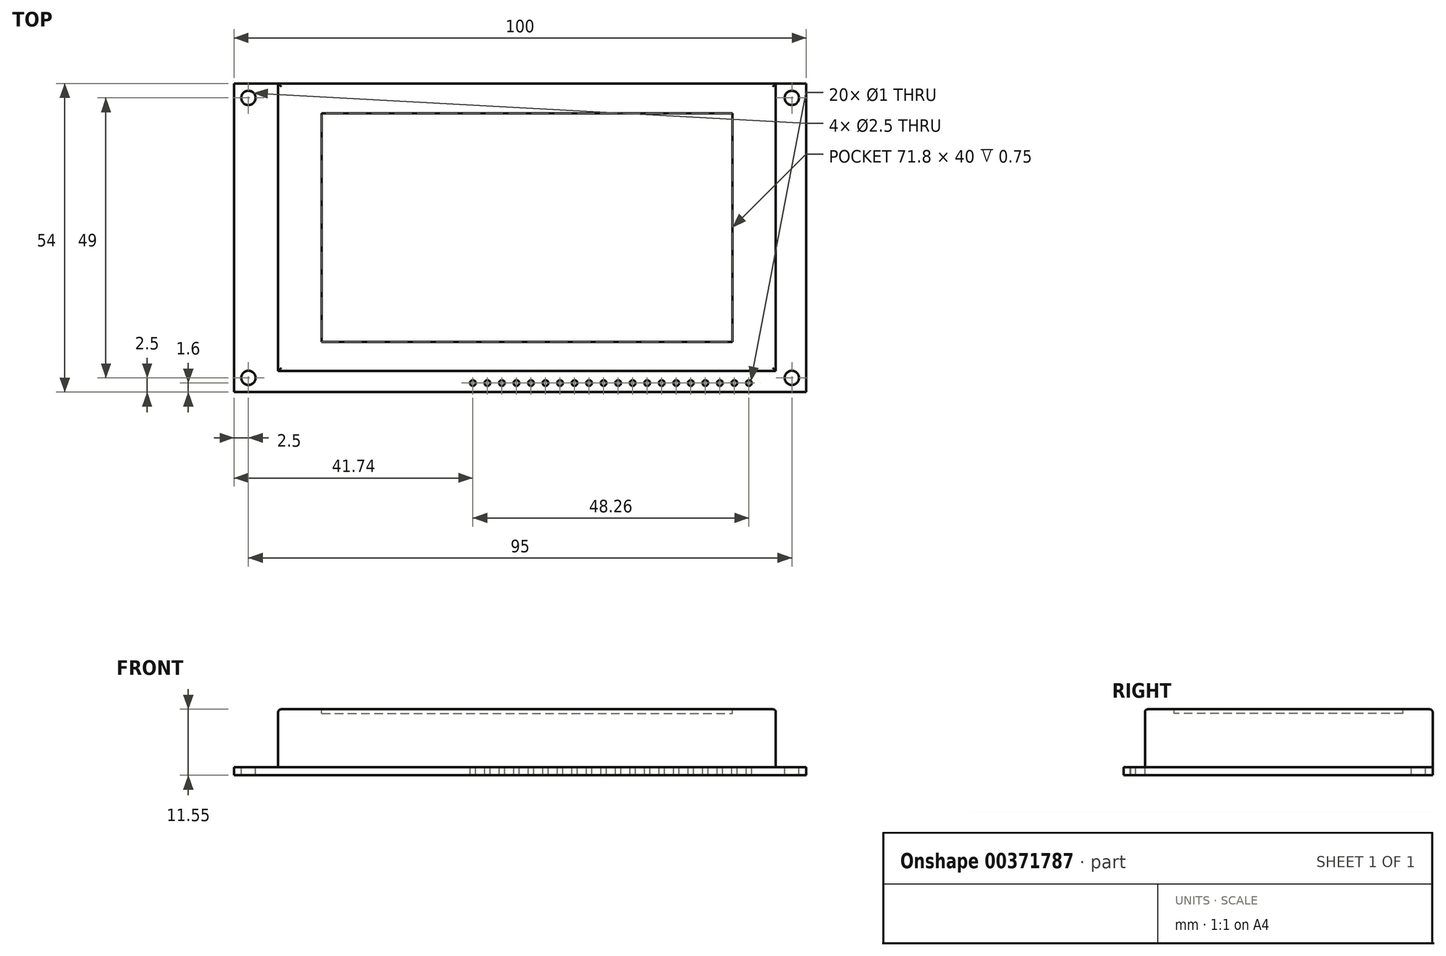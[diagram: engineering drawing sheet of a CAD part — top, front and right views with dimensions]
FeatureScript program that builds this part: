
annotation { "Feature Type Name" : "Feature", "Feature Type Description" : "" }
export const myFeature = defineFeature(function(context is Context, id is Id, definition is map)
    precondition{}
    {
        {
            var Q0;
            Q0=qCreatedBy(makeId("Top.planeOp"),FACE);
            var sketch = newSketch(context, id + "F0", { "sketchPlane" : qUnion([Q0])});
            skLineSegment(sketch, "E0.bottom", {"start": v(0, 0) * mm, "end": v(100, 0) * mm});
            skLineSegment(sketch, "E0.top", {"start": v(0, 54) * mm, "end": v(100, 54) * mm});
            skLineSegment(sketch, "E0.left", {"start": v(0, 0) * mm, "end": v(0, 54) * mm});
            skLineSegment(sketch, "E0.right", {"start": v(100, 0) * mm, "end": v(100, 54) * mm});
            skSolve(sketch);
        }
        {
            var Q0;
            Q0=makeQuery(id+"F0.imprint","IMPRINT",FACE,{"disambiguationData":[TD([[makeQuery(id+"F0.imprint","IMPRINT",EDGE,{"derivedFrom":sQuery(id+"F0.wireOp",EDGE,"E0.bottom")}),1.0]])]});
            extrude(context, id + "F1", {"entities" : qUnion([Q0]), "depth" : 1.45 * mm});
        }
        {
            var Q0;
            Q0=makeQuery(id+"F1.opExtrude","CAP_FACE",FACE,{"disambiguationData":[OSD([sQuery(id+"F0.wireOp",EDGE,"E0.bottom"),sQuery(id+"F0.wireOp",EDGE,"E0.top"),sQuery(id+"F0.wireOp",EDGE,"E0.left"),sQuery(id+"F0.wireOp",EDGE,"E0.right")])],"isStart":false});
            var sketch = newSketch(context, id + "F2", { "sketchPlane" : qUnion([Q0])});
            skLineSegment(sketch, "E1.bottom", {"start": v(7.7, 54) * mm, "end": v(94.7, 54) * mm});
            skLineSegment(sketch, "E1.top", {"start": v(7.7, 3.7) * mm, "end": v(94.7, 3.7) * mm});
            skLineSegment(sketch, "E1.left", {"start": v(7.7, 54) * mm, "end": v(7.7, 3.7) * mm});
            skLineSegment(sketch, "E1.right", {"start": v(94.7, 54) * mm, "end": v(94.7, 3.7) * mm});
            skSolve(sketch);
        }
        {
            var Q0;
            Q0=makeQuery(id+"F2.imprint","IMPRINT",FACE,{"disambiguationData":[TD([[makeQuery(id+"F2.imprint","IMPRINT",EDGE,{"derivedFrom":sQuery(id+"F2.wireOp",EDGE,"E1.bottom")}),-1.0]])]});
            extrude(context, id + "F3", {"entities" : qUnion([Q0]), "operationType" : NewBodyOperationType.ADD, "depth" : 10.1 * mm});
        }
        {
            var Q0;
            Q0=makeQuery(id+"F1.opExtrude","CAP_FACE",FACE,{"disambiguationData":[OSD([sQuery(id+"F0.wireOp",EDGE,"E0.bottom"),sQuery(id+"F0.wireOp",EDGE,"E0.top"),sQuery(id+"F0.wireOp",EDGE,"E0.left"),sQuery(id+"F0.wireOp",EDGE,"E0.right")])],"isStart":false});
            var sketch = newSketch(context, id + "F4", { "sketchPlane" : qUnion([Q0])});
            skLineSegment(sketch, "E2.bottom", {"start": v(2.5, 51.5) * mm, "end": v(97.5, 51.5) * mm, "construction": true});
            skLineSegment(sketch, "E2.top", {"start": v(2.5, 2.5) * mm, "end": v(97.5, 2.5) * mm, "construction": true});
            skLineSegment(sketch, "E2.left", {"start": v(2.5, 51.5) * mm, "end": v(2.5, 2.5) * mm, "construction": true});
            skLineSegment(sketch, "E2.right", {"start": v(97.5, 51.5) * mm, "end": v(97.5, 2.5) * mm, "construction": true});
            skCircle(sketch, "E3", {"center": v(2.5, 51.5) * mm, "radius": 1.25 * mm});
            skCircle(sketch, "E4", {"center": v(2.5, 2.5) * mm, "radius": 1.25 * mm});
            skCircle(sketch, "E5", {"center": v(97.5, 2.5) * mm, "radius": 1.25 * mm});
            skCircle(sketch, "E6", {"center": v(97.5, 51.5) * mm, "radius": 1.25 * mm});
            skSolve(sketch);
        }
        {
            var Q0;
            Q0 = qSketchRegion(id + "F4", true);
            extrude(context, id + "F5", {"entities" : qUnion([Q0]), "operationType" : NewBodyOperationType.REMOVE, "endBound" : BoundingType.THROUGH_ALL, "oppositeDirection" : true, "depth" : 25 * mm});
        }
        {
            var Q0;
            Q0=makeQuery(id+"F3.opExtrude","CAP_FACE",FACE,{"disambiguationData":[OSD([sQuery(id+"F2.wireOp",EDGE,"E1.bottom"),sQuery(id+"F2.wireOp",EDGE,"E1.top"),sQuery(id+"F2.wireOp",EDGE,"E1.left"),sQuery(id+"F2.wireOp",EDGE,"E1.right")])],"isStart":false});
            var sketch = newSketch(context, id + "F6", { "sketchPlane" : qUnion([Q0])});
            skLineSegment(sketch, "E7.bottom", {"start": v(15.3, 48.8) * mm, "end": v(87.1, 48.8) * mm});
            skLineSegment(sketch, "E7.top", {"start": v(15.3, 8.8) * mm, "end": v(87.1, 8.8) * mm});
            skLineSegment(sketch, "E7.left", {"start": v(15.3, 48.8) * mm, "end": v(15.3, 8.8) * mm});
            skLineSegment(sketch, "E7.right", {"start": v(87.1, 48.8) * mm, "end": v(87.1, 8.8) * mm});
            skLineSegment(sketch, "E8", {"start": v(87.1, 8.8) * mm, "end": v(15.3, 48.8) * mm, "construction": true});
            skPoint(sketch, "E9", {"position": v(51.2, 28.8) * mm});
            skSolve(sketch);
        }
        {
            var Q0;
            Q0=makeQuery(id+"F3.opExtrude","CAP_EDGE",EDGE,{"disambiguationData":[OSD([sQuery(id+"F2.wireOp",EDGE,"E1.left")])],"isStart":false});
            var Q1;
            Q1=makeQuery(id+"F3.opExtrude","CAP_EDGE",EDGE,{"disambiguationData":[OSD([sQuery(id+"F2.wireOp",EDGE,"E1.bottom")])],"isStart":false});
            var Q2;
            Q2=makeQuery(id+"F3.opExtrude","CAP_EDGE",EDGE,{"disambiguationData":[OSD([sQuery(id+"F2.wireOp",EDGE,"E1.top")])],"isStart":false});
            var Q3;
            Q3=makeQuery(id+"F3.opExtrude","CAP_EDGE",EDGE,{"disambiguationData":[OSD([sQuery(id+"F2.wireOp",EDGE,"E1.right")])],"isStart":false});
            fillet(context, id + "F7", {"entities" : qUnion([Q0, Q1, Q2, Q3]), "radius" : 0.5 * mm, "tangentPropagation" : true, "allowEdgeOverflow" : false});
        }
        {
            var Q0;
            Q0=makeQuery(id+"F6.imprint","IMPRINT",FACE,{"disambiguationData":[TD([[makeQuery(id+"F6.imprint","IMPRINT",EDGE,{"derivedFrom":sQuery(id+"F6.wireOp",EDGE,"E7.bottom")}),-1.0]])]});
            extrude(context, id + "F8", {"entities" : qUnion([Q0]), "operationType" : NewBodyOperationType.REMOVE, "oppositeDirection" : true, "depth" : .75 * mm});
        }
        {
            var Q0;
            Q0=makeQuery(id+"F1.opExtrude","CAP_FACE",FACE,{"disambiguationData":[OSD([sQuery(id+"F0.wireOp",EDGE,"E0.bottom"),sQuery(id+"F0.wireOp",EDGE,"E0.top"),sQuery(id+"F0.wireOp",EDGE,"E0.left"),sQuery(id+"F0.wireOp",EDGE,"E0.right")])],"isStart":false});
            var sketch = newSketch(context, id + "F9", { "sketchPlane" : qUnion([Q0])});
            skCircle(sketch, "E10", {"center": v(90, 1.6) * mm, "radius": 0.5 * mm});
            skCircle(sketch, "E11.1.0.0", {"center": v(87.46, 1.6) * mm, "radius": 0.5 * mm});
            skCircle(sketch, "E11.2.0.0", {"center": v(84.92, 1.6) * mm, "radius": 0.5 * mm});
            skCircle(sketch, "E11.3.0.0", {"center": v(82.38, 1.6) * mm, "radius": 0.5 * mm});
            skCircle(sketch, "E11.4.0.0", {"center": v(79.84, 1.6) * mm, "radius": 0.5 * mm});
            skCircle(sketch, "E11.5.0.0", {"center": v(77.3, 1.6) * mm, "radius": 0.5 * mm});
            skCircle(sketch, "E11.6.0.0", {"center": v(74.76, 1.6) * mm, "radius": 0.5 * mm});
            skCircle(sketch, "E11.7.0.0", {"center": v(72.22, 1.6) * mm, "radius": 0.5 * mm});
            skCircle(sketch, "E11.8.0.0", {"center": v(69.68, 1.6) * mm, "radius": 0.5 * mm});
            skCircle(sketch, "E11.9.0.0", {"center": v(67.14, 1.6) * mm, "radius": 0.5 * mm});
            skCircle(sketch, "E11.10.0.0", {"center": v(64.6, 1.6) * mm, "radius": 0.5 * mm});
            skCircle(sketch, "E11.11.0.0", {"center": v(62.06, 1.6) * mm, "radius": 0.5 * mm});
            skCircle(sketch, "E11.12.0.0", {"center": v(59.52, 1.6) * mm, "radius": 0.5 * mm});
            skCircle(sketch, "E11.13.0.0", {"center": v(56.98, 1.6) * mm, "radius": 0.5 * mm});
            skCircle(sketch, "E11.14.0.0", {"center": v(54.44, 1.6) * mm, "radius": 0.5 * mm});
            skCircle(sketch, "E11.15.0.0", {"center": v(51.9, 1.6) * mm, "radius": 0.5 * mm});
            skCircle(sketch, "E11.16.0.0", {"center": v(49.36, 1.6) * mm, "radius": 0.5 * mm});
            skCircle(sketch, "E11.17.0.0", {"center": v(46.82, 1.6) * mm, "radius": 0.5 * mm});
            skCircle(sketch, "E11.18.0.0", {"center": v(44.28, 1.6) * mm, "radius": 0.5 * mm});
            skCircle(sketch, "E11.19.0.0", {"center": v(41.74, 1.6) * mm, "radius": 0.5 * mm});
            skLineSegment(sketch, "E11.direction1", {"start": v(90, 1.6) * mm, "end": v(87.46, 1.6) * mm, "construction": true});
            skSolve(sketch);
        }
        {
            var Q0;
            Q0 = qSketchRegion(id + "F9", true);
            extrude(context, id + "F10", {"entities" : qUnion([Q0]), "operationType" : NewBodyOperationType.REMOVE, "endBound" : BoundingType.THROUGH_ALL, "oppositeDirection" : true, "depth" : 25 * mm});
        }
    });
